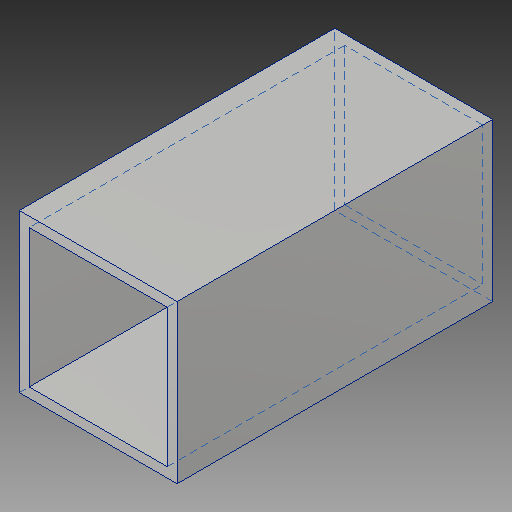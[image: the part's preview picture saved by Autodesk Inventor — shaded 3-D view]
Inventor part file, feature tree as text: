
AUTODESK INVENTOR PART (.ipt)
format: ipt  version: 2019 (Build 230136000, 136)  size: 104,448 bytes
history: native  units: in
note: dims shown in document units (in); Inventor stores cm internally (conversion verified against a paired STEP export)
features: extrude x1, sketch x1
ambient origin geometry x8: Origin, YZ Plane, XZ Plane, XY Plane, X Axis, Y Axis, Z Axis, Center Point
bodies: Solid1 (feature_tree)
feature tree (2):
  extrude  "Extrusion1"  Depth=0.125in
  sketch  "Sketch1"  dims[d0=2.0in d1=0.125in d2=4.0in d3=0.0in d11=2.0in d12=0.125in]
